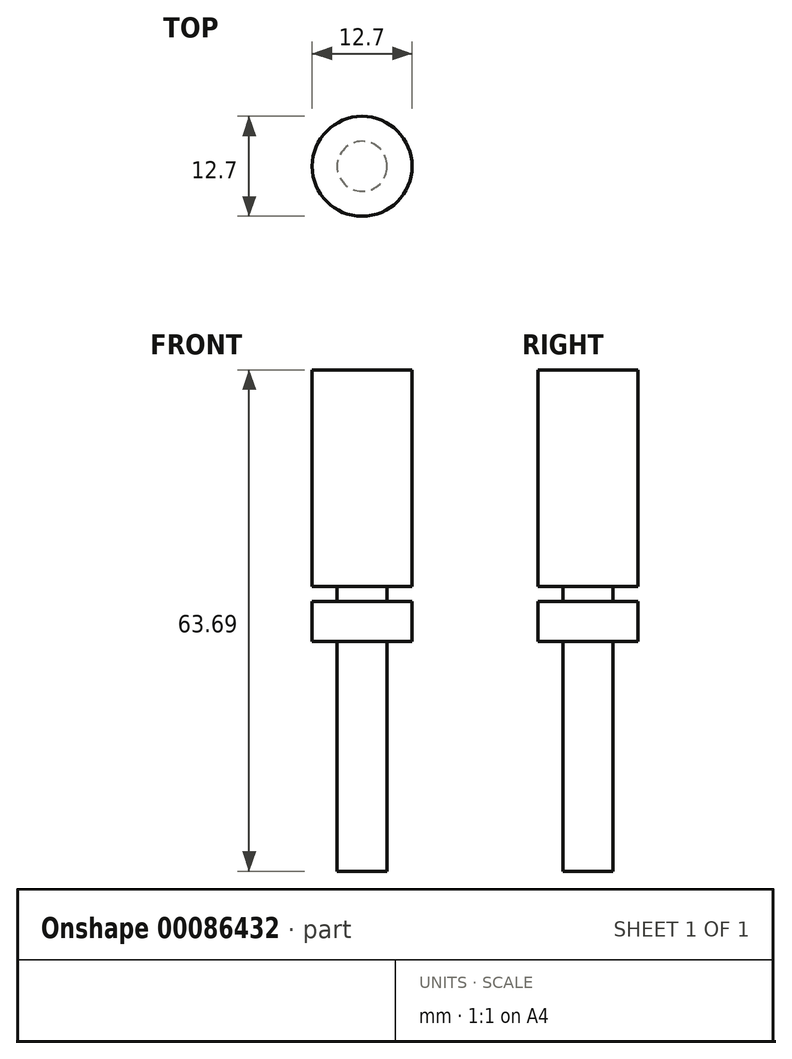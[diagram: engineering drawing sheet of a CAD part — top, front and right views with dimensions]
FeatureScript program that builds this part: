
annotation { "Feature Type Name" : "Feature", "Feature Type Description" : "" }
export const myFeature = defineFeature(function(context is Context, id is Id, definition is map)
    precondition{}
    {
        {
            var Q0;
            Q0=qCreatedBy(makeId("Top.planeOp"),FACE);
            var sketch = newSketch(context, id + "F0", { "sketchPlane" : qUnion([Q0])});
            skCircle(sketch, "E0", {"center": v(0, 0) * mm, "radius": 3.18 * mm});
            skSolve(sketch);
        }
        {
            var Q0;
            Q0=qCreatedBy(makeId("Top.planeOp"),FACE);
            var sketch = newSketch(context, id + "F1", { "sketchPlane" : qUnion([Q0])});
            skCircle(sketch, "E1", {"center": v(0, 0) * mm, "radius": 6.35 * mm});
            skSolve(sketch);
        }
        {
            var Q0;
            Q0 = qSketchRegion(id + "F0", true);
            extrude(context, id + "F2", {"entities" : qUnion([Q0]), "endBound" : BoundingType.SYMMETRIC, "depth" : 63.5 * mm});
        }
        {
            var Q0;
            Q0 = qSketchRegion(id + "F1", true);
            extrude(context, id + "F3", {"entities" : qUnion([Q0]), "operationType" : NewBodyOperationType.ADD, "endBound" : BoundingType.SYMMETRIC, "depth" : 5.08 * mm});
        }
        {
            var Q0;
            Q0=qCreatedBy(makeId("Top.planeOp"),FACE);
            cPlane(context, id + "F4", {"entities" : qUnion([Q0]), "cplaneType" : CPlaneType.OFFSET, "offset" : 4.44 * mm, "width" : 152.4 * mm, "height" : 152.4 * mm});
        }
        {
            var Q0;
            Q0=qCreatedBy(id+"F4.planeOp",FACE);
            var sketch = newSketch(context, id + "F5", { "sketchPlane" : qUnion([Q0])});
            skCircle(sketch, "E2.0", {"center": v(0, 0) * mm, "radius": 6.35 * mm});
            skSolve(sketch);
        }
        {
            var Q0;
            Q0 = qSketchRegion(id + "F5", true);
            extrude(context, id + "F6", {"entities" : qUnion([Q0]), "operationType" : NewBodyOperationType.ADD, "depth" : 27.5 * mm});
        }
    });
